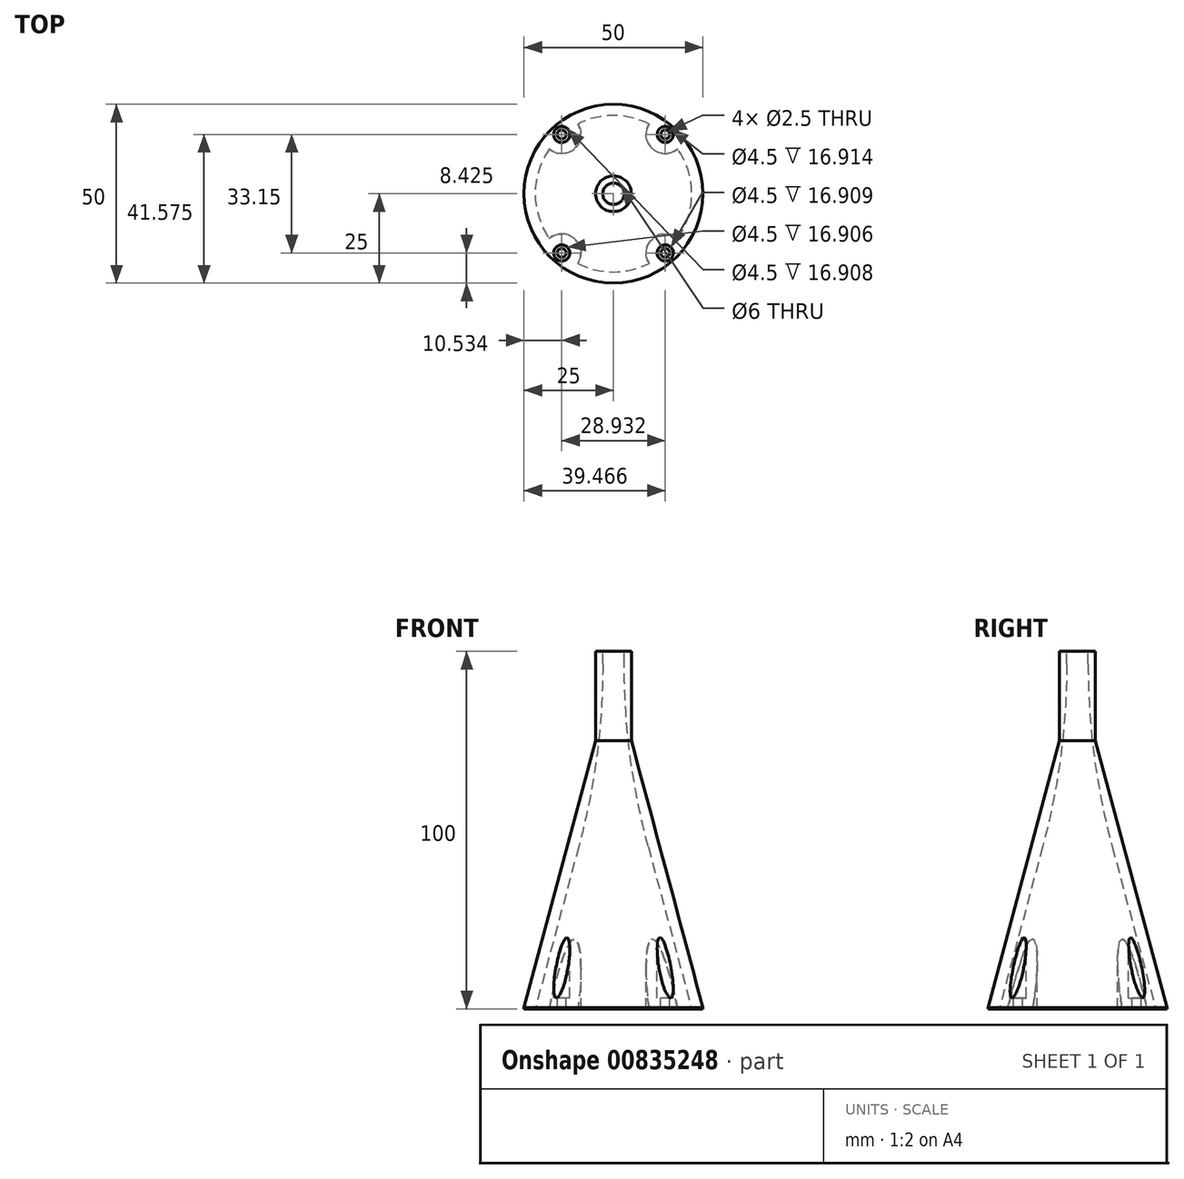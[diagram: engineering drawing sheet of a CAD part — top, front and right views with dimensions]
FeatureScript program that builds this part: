
annotation { "Feature Type Name" : "Feature", "Feature Type Description" : "" }
export const myFeature = defineFeature(function(context is Context, id is Id, definition is map)
    precondition{}
    {
        {
            var Q0;
            Q0=qCreatedBy(makeId("Top.planeOp"),FACE);
            var sketch = newSketch(context, id + "F0", { "sketchPlane" : qUnion([Q0])});
            skCircle(sketch, "E0", {"center": v(0, 0) * mm, "radius": 25 * mm});
            skSolve(sketch);
        }
        {
            var Q0;
            Q0=makeQuery(id+"F0.imprint","IMPRINT",FACE,{"disambiguationData":[TD([[makeQuery(id+"F0.imprint","IMPRINT",EDGE,{"derivedFrom":sQuery(id+"F0.wireOp",EDGE,"E0")}),1.0]])]});
            extrude(context, id + "F1", {"entities" : qUnion([Q0]), "depth" : 20 * mm, "offsetDistance" : 25 * mm});
        }
        {
            var Q0;
            Q0=makeQuery(id+"F1.opExtrude","CAP_FACE",FACE,{"disambiguationData":[OSD([sQuery(id+"F0.wireOp",EDGE,"E0")])],"isStart":false});
            var sketch = newSketch(context, id + "F2", { "sketchPlane" : qUnion([Q0])});
            skCircle(sketch, "E1", {"center": v(-14.47, -16.57) * mm, "radius": 3 * mm});
            skPoint(sketch, "E1.first.point", {"position": v(-16.44, -18.84) * mm});
            skPoint(sketch, "E1.second.point", {"position": v(-12.8, -14.08) * mm});
            skPoint(sketch, "E1.third.point", {"position": v(-15.23, -13.67) * mm});
            skCircle(sketch, "E2", {"center": v(-14.47, -16.57) * mm, "radius": 1.25 * mm});
            skCircle(sketch, "E3.MirrorC", {"center": v(-14.47, 16.57) * mm, "radius": 1.25 * mm});
            skCircle(sketch, "E4.MirrorC", {"center": v(-14.47, 16.57) * mm, "radius": 3 * mm});
            skCircle(sketch, "E5.MirrorC", {"center": v(14.47, -16.57) * mm, "radius": 1.25 * mm});
            skCircle(sketch, "E6.MirrorC", {"center": v(14.47, -16.57) * mm, "radius": 3 * mm});
            skCircle(sketch, "E7.MirrorC", {"center": v(14.47, 16.57) * mm, "radius": 3 * mm});
            skCircle(sketch, "E8.MirrorC", {"center": v(14.47, 16.57) * mm, "radius": 1.25 * mm});
            skSolve(sketch);
        }
        {
            var Q0;
            {var subQ3=sQuery(id+"F2.wireOp",EDGE,"E1");Q0=makeQuery(id+"F2.imprint","IMPRINT",FACE,{"disambiguationData":[TD([[makeQuery(id+"F2.imprint","IMPRINT",EDGE,{"derivedFrom":subQ3}),-1.0]])]});}
            var Q1;
            Q1=makeQuery(id+"F2.imprint","IMPRINT",FACE,{"disambiguationData":[TD([[makeQuery(id+"F2.imprint","IMPRINT",EDGE,{"derivedFrom":sQuery(id+"F2.wireOp",EDGE,"E1")}),1.0]])]});
            var Q2;
            Q2=makeQuery(id+"F2.imprint","IMPRINT",FACE,{"disambiguationData":[TD([[makeQuery(id+"F2.imprint","IMPRINT",EDGE,{"derivedFrom":sQuery(id+"F2.wireOp",EDGE,"E2")}),1.0]])]});
            var Q3;
            Q3=makeQuery(id+"F2.imprint","IMPRINT",FACE,{"disambiguationData":[TD([[makeQuery(id+"F2.imprint","IMPRINT",EDGE,{"derivedFrom":sQuery(id+"F2.wireOp",EDGE,"E5.MirrorC")}),-1.0]])]});
            var Q4;
            Q4=makeQuery(id+"F2.imprint","IMPRINT",FACE,{"disambiguationData":[TD([[makeQuery(id+"F2.imprint","IMPRINT",EDGE,{"derivedFrom":sQuery(id+"F2.wireOp",EDGE,"E5.MirrorC")}),1.0]])]});
            var Q5;
            Q5=makeQuery(id+"F2.imprint","IMPRINT",FACE,{"disambiguationData":[TD([[makeQuery(id+"F2.imprint","IMPRINT",EDGE,{"derivedFrom":sQuery(id+"F2.wireOp",EDGE,"E7.MirrorC")}),1.0]])]});
            var Q6;
            Q6=makeQuery(id+"F2.imprint","IMPRINT",FACE,{"disambiguationData":[TD([[makeQuery(id+"F2.imprint","IMPRINT",EDGE,{"derivedFrom":sQuery(id+"F2.wireOp",EDGE,"E8.MirrorC")}),1.0]])]});
            var Q7;
            Q7=makeQuery(id+"F2.imprint","IMPRINT",FACE,{"disambiguationData":[TD([[makeQuery(id+"F2.imprint","IMPRINT",EDGE,{"derivedFrom":sQuery(id+"F2.wireOp",EDGE,"E3.MirrorC")}),1.0]])]});
            var Q8;
            Q8=makeQuery(id+"F2.imprint","IMPRINT",FACE,{"disambiguationData":[TD([[makeQuery(id+"F2.imprint","IMPRINT",EDGE,{"derivedFrom":sQuery(id+"F2.wireOp",EDGE,"E3.MirrorC")}),-1.0]])]});
            extrude(context, id + "F3", {"entities" : qUnion([Q0, Q1, Q2, Q3, Q4, Q5, Q6, Q7, Q8]), "operationType" : NewBodyOperationType.ADD, "depth" : 55 * mm, "offsetDistance" : 25 * mm});
        }
        {
            var Q0;
            Q0=makeQuery(id+"F3.opExtrude","CAP_FACE",FACE,{"disambiguationData":[OSD([sQuery(id+"F0.wireOp",EDGE,"E0")])],"isStart":false});
            chamfer(context, id + "F4", {"entities" : qUnion([Q0]), "chamferType" : ChamferType.OFFSET_ANGLE, "width" : 20 * mm, "oppositeDirection" : false, "angle" : 75 * degree, "tangentPropagation" : true});
        }
        {
            var Q0;
            Q0=sQuery(id+"F2.wireOp",VERTEX,"E7.MirrorC.center");
            var Q1;
            Q1=sQuery(id+"F2.wireOp",VERTEX,"E5.MirrorC.center");
            var Q2;
            Q2=sQuery(id+"F2.wireOp",VERTEX,"E1.center");
            var Q3;
            Q3=sQuery(id+"F2.wireOp",VERTEX,"E3.MirrorC.center");
            var Q4;
            Q4=makeQuery(id+"F1.opExtrude","SWEPT_BODY",BODY,{"disambiguationData":[OSD([sQuery(id+"F0.wireOp",EDGE,"E0")])]});
            hole(context, id + "F5", {"style" : HoleStyle.C_BORE, "endStyle" : HoleEndStyle.THROUGH, "holeDiameter" : 2.5 * mm, "cBoreDiameter" : 4.5 * mm, "cBoreDepth" : .1 * mm, "majorDiameter" : 5 * mm, "isTappedThrough" : true, "tappedDepth" : 12 * mm, "tapClearance" : 3, "locations" : qUnion([Q0, Q1, Q2, Q3]), "scope" : qUnion([Q4])});
        }
        {
            var Q0;
            Q0=makeQuery(id+"F3.opExtrude","CAP_FACE",FACE,{"disambiguationData":[OSD([sQuery(id+"F0.wireOp",EDGE,"E0")])],"isStart":false});
            extrude(context, id + "F6", {"entities" : qUnion([Q0]), "operationType" : NewBodyOperationType.ADD, "depth" : 25 * mm, "offsetDistance" : 25 * mm});
        }
        {
            var Q0;
            Q0=makeQuery(id+"F6.opExtrude","CAP_FACE",FACE,{"disambiguationData":[OSD([sQuery(id+"F0.wireOp",EDGE,"E0")])],"isStart":false});
            var sketch = newSketch(context, id + "F7", { "sketchPlane" : qUnion([Q0])});
            skCircle(sketch, "E9", {"center": v(0, 0) * mm, "radius": 3 * mm});
            skSolve(sketch);
        }
        {
            var Q0;
            Q0=makeQuery(id+"F1.opExtrude","CAP_FACE",FACE,{"disambiguationData":[OSD([sQuery(id+"F0.wireOp",EDGE,"E0")])],"isStart":true});
            var Q1;
            Q1=makeQuery(id+"F1.opExtrude","SWEPT_BODY",BODY,{"disambiguationData":[OSD([sQuery(id+"F0.wireOp",EDGE,"E0")])]});
            shell(context, id + "F8", {"entities" : qUnion([Q0]), "parts" : qUnion([Q1]), "thickness" : 3.1 * mm});
        }
        {
            var Q0;
            Q0=makeQuery(id+"F7.imprint","IMPRINT",FACE,{"disambiguationData":[TD([[makeQuery(id+"F7.imprint","IMPRINT",EDGE,{"derivedFrom":sQuery(id+"F7.wireOp",EDGE,"E9")}),1.0]])]});
            var Q1;
            Q1=sQuery(id+"F7.wireOp",EDGE,"E9");
            extrude(context, id + "F9", {"entities" : qUnion([Q0]), "operationType" : NewBodyOperationType.REMOVE, "surfaceEntities" : qUnion([Q1]), "oppositeDirection" : true, "depth" : 30 * mm, "offsetDistance" : 25 * mm});
        }
        {
            var Q0;
            {var subQ0=sQuery(id+"F0.wireOp",EDGE,"E0");Q0=makeQuery(id+"F9.boolean.opBoolean","INTERSECT",EDGE,{"derivedFrom":[makeQuery(id+"F8.opShell","OFFSET_FACE",FACE,{"disambiguationData":[OSD([subQ0]),TDD([makeQuery(id+"F4.opChamfer","BLEND_FACE",FACE,{"disambiguationData":[OSD([subQ0])]})])]}),makeQuery(id+"F9.opExtrude","SWEPT_FACE",FACE,{"disambiguationData":[OSD([sQuery(id+"F7.wireOp",EDGE,"E9")])]})]});}
            fillet(context, id + "F10", {"entities" : qUnion([Q0]), "radius" : 197 * mm, "tangentPropagation" : true, "allowEdgeOverflow" : false});
        }
    });
